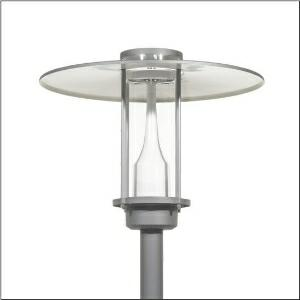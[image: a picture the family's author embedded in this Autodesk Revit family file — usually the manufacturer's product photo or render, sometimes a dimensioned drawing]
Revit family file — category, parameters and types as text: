
# Revit family: city-light_plus_iq___pl1_2s_5xa5275cf14h_efc5
name_source: partatom
category: Lighting Fixtures
units: mm (PartAtom-declared; Revit-internal decimal feet)

## family parameters
Cut with Voids When Loaded = No
Host = Face
Light Source = No
Part Type = Normal
Room Calculation Point = No
Round Connector Dimension = Use Diameter
Shared = No

## types (1)
- --- (1 x LED, 2840 lm, 23.9 W, 2200K)
    Apparent Load = 24 VA
    CIE Flux Codes = 23 63 93 97 100
    Color Rendering = 70
    Color Temperature = 2200K
    Default Elevation = 1800 mm
    Description = City-Light Plus iQ, mast luminaire, Module 540 iQ-SR, primary light control with 3 zone facetted reflector, of plastic, silver coated, highly specular, structured, primary optical cover: cover, of PMMA, transparent, light distribution: PL1.2s, light emission: direct distribution, primary light characteristic: symmetric, installation type: post-top, LED, High Power LED, rated luminous flux: 2.840lm, luminous efficacy: 119lm/W, light colour: 722, colour temperature: 2200K, control gear: iQ Street-Remote, control: pre-setting: logarithmic dimming characteristic, Street-Remote, Auto-Match, Temp-Guard, Lumen-Switch, Night-Set, Smart-Wire, Light-Fading, Desk-Remote (wireless, voltage-free reading and setting of iQ features in the workshop via application-optimized NFC function/RFID function), optimised constant luminous flux control (CLO 2.0), with terminal, 6-pole, max. 2.5mm², mains connection: 230..240V, AC, 50/60Hz, start of lifetime: 24W, end of service life: 26W, reduction: 12W, luminaire housing, upper part, of glass-fibre reinforced polyester, coated, Siteco® metallic grey (DB 702S), diameter: 750mm, height: 590mm, spigot size: d x l = 76 x 70mm (post-top) | with reducer (optional accessory) 60 x 70mm, mounting height: 3..5m, post-top mast mounting element, of diecast aluminium, coated, Siteco® metallic grey (DB 702S), Module 540 iQ-SR, traffic white (RAL 9016), equipment: standard, protection rating (complete): IP65, insulation class (complete): insulation class II (safety insulation), certification: CE, ENEC, VDE, packaging unit: 1 piece

Light Distribution: PL1.2s
    Height = 590 mm
    Lamp = 1 x LED
    Lamp Light Flux = 2840 lm
    Lamp Power = 23.9 W
    Lamp count = 1
    Length = 750 mm
    Luminous efficacy = 119 lm/W
    Manufacturer = Siteco
    ModVariant = No
    Model = 5XA5275CF14H
    Number of Poles = 1
    OnlyDefault = Yes
    Power Factor = 1
    Product Name = City-Light Plus iQ | PL1.2s
    Product group = mast luminaire | pylon top
    ProductGroupID = 6100
    Protection Class = Protection class II
    Protection Degree = IP 65
    RLX_Detail_Level = 1
    RLX_Emergency_Light_Flux = 0 lm
    RLX_Emergency_Type = 0
    RLX_Emergency_Type_DB = No
    RlxData = <blob elided: 33293 chars, md5=52995081>
    Socket = socket
    Standby Power = 0 W
    System Light Flux = 2840 lm
    System Power = 24 W
    Type Comments = factory setting: luminous flux: 100 % | dim-lin: 254 | 499 mA
    Type Image = l_1006456.jpg
    URL = http://relux.com
    VarID = @adj_145594
    Voltage = 0 V
    Weight = 0.00 kg
    Width = 0 mm  [stored 0 ft]

note: [stored X ft] marks values corroborated as IEEE doubles in the binary element streams (Revit-internal decimal feet)

## geometry (parser evidence)
native form markers: Blend x4, Sweep x11
no freeform markers — native parametric forms only
